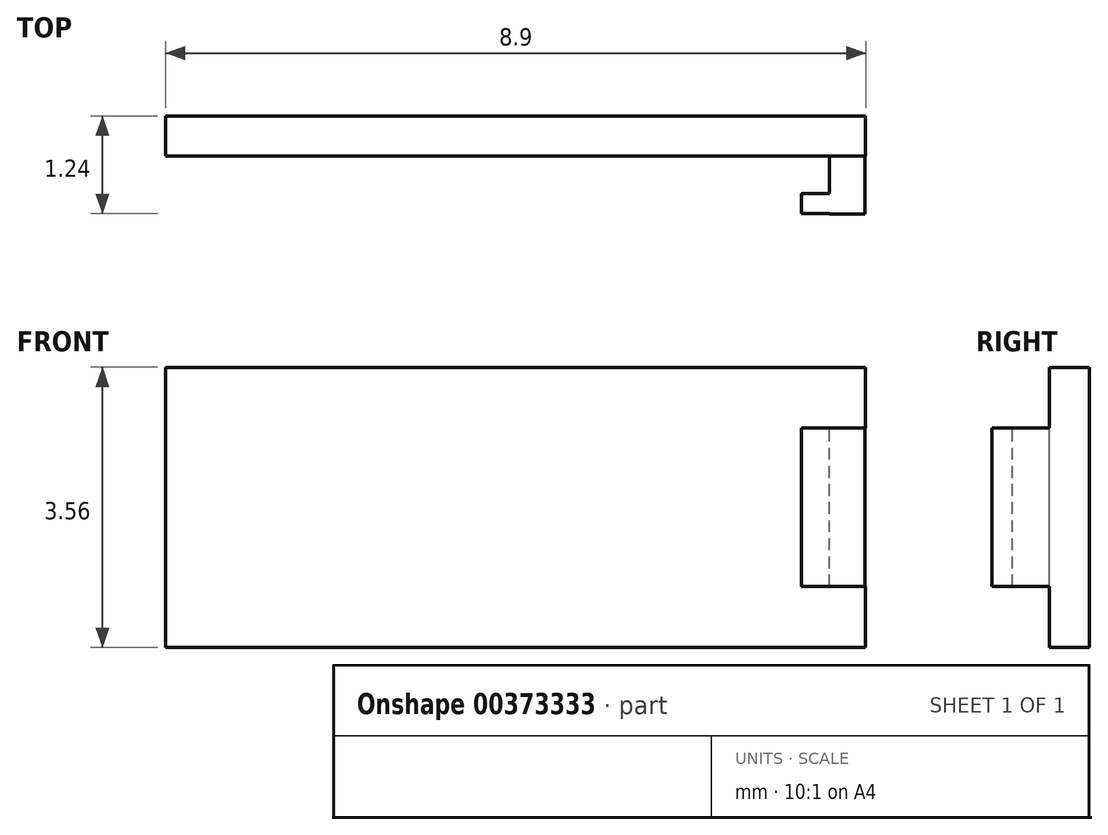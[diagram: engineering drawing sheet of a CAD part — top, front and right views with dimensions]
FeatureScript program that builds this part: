
annotation { "Feature Type Name" : "Feature", "Feature Type Description" : "" }
export const myFeature = defineFeature(function(context is Context, id is Id, definition is map)
    precondition{}
    {
        {
            var Q0;
            Q0=qCreatedBy(makeId("Front.planeOp"),FACE);
            var sketch = newSketch(context, id + "F0", { "sketchPlane" : qUnion([Q0])});
            skLineSegment(sketch, "E0.bottom", {"start": v(-4.44, -1.78) * mm, "end": v(4.45, -1.78) * mm});
            skLineSegment(sketch, "E0.top", {"start": v(-4.45, 1.78) * mm, "end": v(4.44, 1.78) * mm});
            skLineSegment(sketch, "E0.left", {"start": v(-4.44, -1.78) * mm, "end": v(-4.45, 1.78) * mm});
            skLineSegment(sketch, "E0.right", {"start": v(4.45, -1.78) * mm, "end": v(4.44, 1.78) * mm});
            skPoint(sketch, "E0.middle", {"position": v(0, 0) * mm});
            skSolve(sketch);
        }
        {
            var Q0;
            Q0 = qSketchRegion(id + "F0", true);
            extrude(context, id + "F1", {"entities" : qUnion([Q0]), "depth" : 0.5 * mm});
        }
        {
            var Q0;
            Q0=makeQuery(id+"F1.opExtrude","CAP_FACE",FACE,{"disambiguationData":[OSD([sQuery(id+"F0.wireOp",EDGE,"E0.bottom"),sQuery(id+"F0.wireOp",EDGE,"E0.top"),sQuery(id+"F0.wireOp",EDGE,"E0.left"),sQuery(id+"F0.wireOp",EDGE,"E0.right")])],"isStart":false});
            var sketch = newSketch(context, id + "F2", { "sketchPlane" : qUnion([Q0])});
            skLineSegment(sketch, "E1.bottom", {"start": v(3.98, -1) * mm, "end": v(4.44, -1) * mm});
            skLineSegment(sketch, "E1.top", {"start": v(3.98, 1) * mm, "end": v(4.44, 1) * mm});
            skLineSegment(sketch, "E1.left", {"start": v(3.98, -1) * mm, "end": v(3.98, 1) * mm});
            skLineSegment(sketch, "E1.right", {"start": v(4.44, -1) * mm, "end": v(4.44, 1) * mm});
            skPoint(sketch, "E1.middle", {"position": v(4.21, 0) * mm});
            skPoint(sketch, "E1.middle.positionSnap0", {"position": v(4.45, 0) * mm});
            skPoint(sketch, "E1.centerSnap0", {"position": v(4.45, 0) * mm});
            skSolve(sketch);
        }
        {
            var Q0;
            Q0 = qSketchRegion(id + "F2", true);
            extrude(context, id + "F3", {"entities" : qUnion([Q0]), "operationType" : NewBodyOperationType.ADD, "depth" : 0.73 * mm});
        }
        {
            var Q0;
            Q0=makeQuery(id+"F3.opExtrude","SWEPT_FACE",FACE,{"disambiguationData":[OSD([sQuery(id+"F2.wireOp",EDGE,"E1.left")])]});
            var sketch = newSketch(context, id + "F4", { "sketchPlane" : qUnion([Q0])});
            skLineSegment(sketch, "E2.bottom", {"start": v(0.98, -1) * mm, "end": v(1.24, -1) * mm});
            skLineSegment(sketch, "E2.top", {"start": v(0.98, 1) * mm, "end": v(1.24, 1) * mm});
            skLineSegment(sketch, "E2.left", {"start": v(0.98, -1) * mm, "end": v(0.98, 1) * mm});
            skLineSegment(sketch, "E2.right", {"start": v(1.24, -1) * mm, "end": v(1.24, 1) * mm});
            skPoint(sketch, "E2.middle", {"position": v(1.11, 0) * mm});
            skPoint(sketch, "E2.middle.positionSnap0", {"position": v(1.24, 0) * mm});
            skPoint(sketch, "E2.centerSnap0", {"position": v(1.24, 0) * mm});
            skSolve(sketch);
        }
        {
            var Q0;
            Q0 = qSketchRegion(id + "F4", true);
            extrude(context, id + "F5", {"entities" : qUnion([Q0]), "operationType" : NewBodyOperationType.ADD, "depth" : 0.36 * mm});
        }
    });
